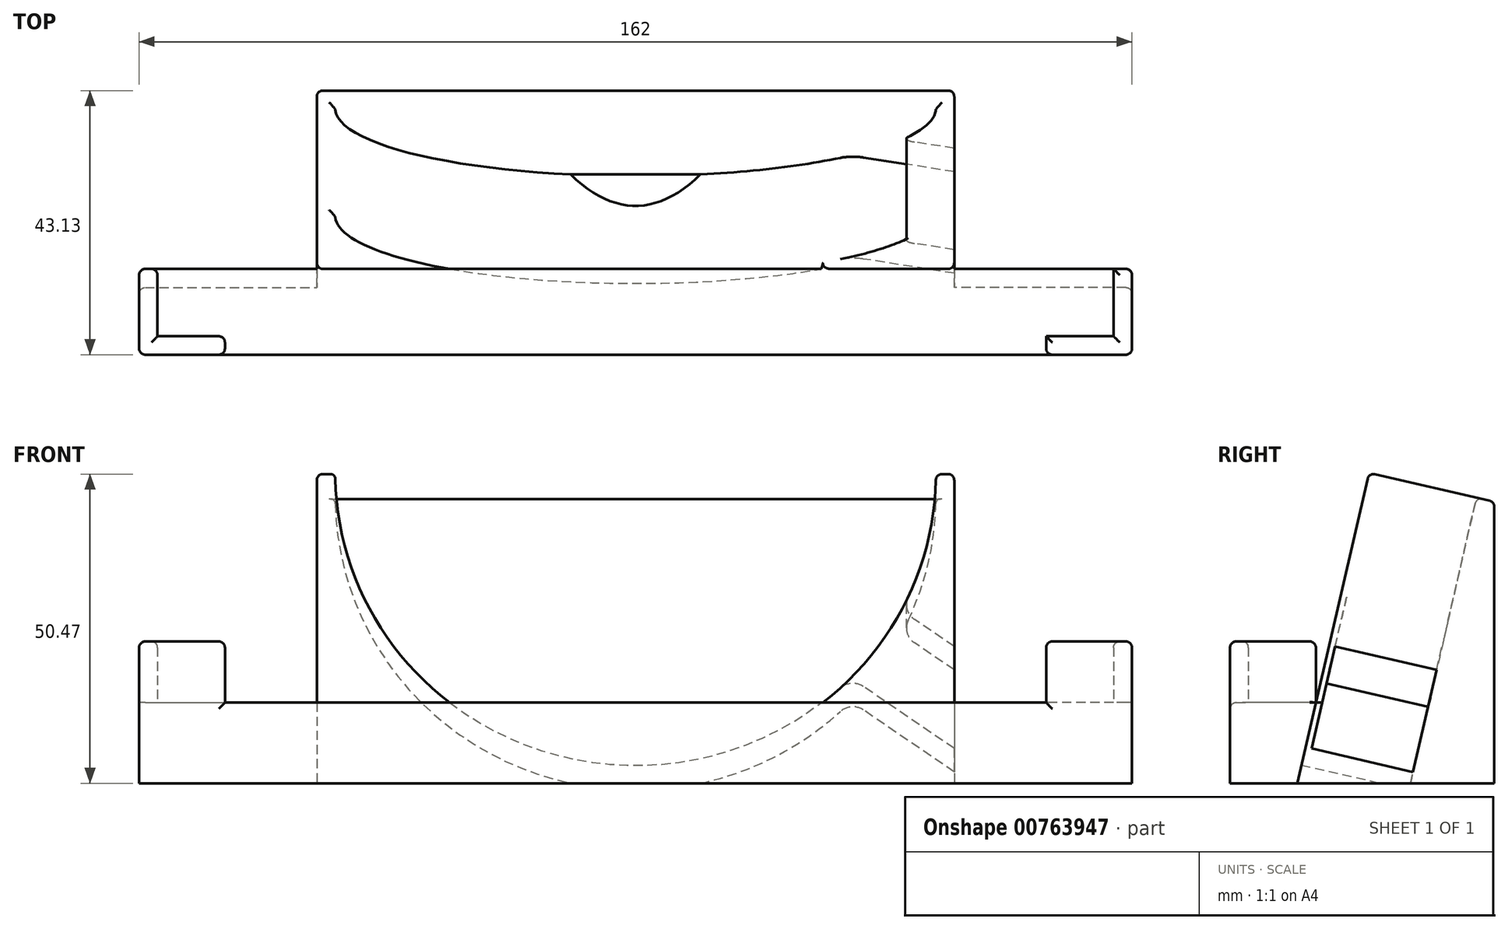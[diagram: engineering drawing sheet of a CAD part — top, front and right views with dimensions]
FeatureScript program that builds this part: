
annotation { "Feature Type Name" : "Feature", "Feature Type Description" : "" }
export const myFeature = defineFeature(function(context is Context, id is Id, definition is map)
    precondition{}
    {
        {
            var Q0;
            Q0=qCreatedBy(makeId("Right.planeOp"),FACE);
            var sketch = newSketch(context, id + "F0", { "sketchPlane" : qUnion([Q0])});
            skLineSegment(sketch, "E0", {"start": v(-55.45, -33.4) * mm, "end": v(107.34, -33.4) * mm});
            skLineSegment(sketch, "E1", {"start": v(-32.06, 67.93) * mm, "end": v(-11.6, 63.2) * mm});
            skLineSegment(sketch, "E2", {"start": v(-11.6, 63.2) * mm, "end": v(-11.6, -33.4) * mm});
            skLineSegment(sketch, "E3", {"start": v(-11.6, 63.2) * mm, "end": v(-33.9, -33.4) * mm});
            skLineSegment(sketch, "E4", {"start": v(-52.42, -20.25) * mm, "end": v(-66.42, -20.25) * mm});
            skLineSegment(sketch, "E5", {"start": v(-66.42, -20.25) * mm, "end": v(-66.42, -33.4) * mm});
            skLineSegment(sketch, "E6", {"start": v(-66.42, -33.4) * mm, "end": v(-47.42, -33.4) * mm});
            skLineSegment(sketch, "E7", {"start": v(-32.06, 67.93) * mm, "end": v(-55.45, -33.4) * mm});
            skLineSegment(sketch, "E8", {"start": v(-43.76, 17.26) * mm, "end": v(-23.3, 12.54) * mm});
            skLineSegment(sketch, "E9", {"start": v(-23.3, 12.54) * mm, "end": v(-23.3, -33.4) * mm});
            skSolve(sketch);
        }
        {
            var Q0;
            {var subQ3=sQuery(id+"F0.wireOp",EDGE,"E9");Q0=makeQuery(id+"F0.imprint","IMPRINT",FACE,{"disambiguationData":[TD([[makeQuery(id+"F0.imprint","IMPRINT",EDGE,{"derivedFrom":subQ3}),-1.0]])]});}
            var Q1;
            {var subQ2=sQuery(id+"F0.wireOp",EDGE,"E8");Q1=makeQuery(id+"F0.imprint","IMPRINT",FACE,{"disambiguationData":[TD([[makeQuery(id+"F0.imprint","IMPRINT",EDGE,{"derivedFrom":subQ2}),-1.0]])]});}
            extrude(context, id + "F1", {"entities" : qUnion([Q0, Q1]), "oppositeDirection" : true, "depth" : 52 * mm, "offsetDistance" : 25 * mm});
        }
        {
            var Q0;
            {var subQ3=sQuery(id+"F0.wireOp",EDGE,"E9");Q0=makeQuery(id+"F0.imprint","IMPRINT",FACE,{"disambiguationData":[TD([[makeQuery(id+"F0.imprint","IMPRINT",EDGE,{"derivedFrom":subQ3}),-1.0]])]});}
            var Q1;
            {var subQ2=sQuery(id+"F0.wireOp",EDGE,"E8");Q1=makeQuery(id+"F0.imprint","IMPRINT",FACE,{"disambiguationData":[TD([[makeQuery(id+"F0.imprint","IMPRINT",EDGE,{"derivedFrom":subQ2}),-1.0]])]});}
            extrude(context, id + "F2", {"entities" : qUnion([Q0, Q1]), "operationType" : NewBodyOperationType.ADD, "depth" : 52 * mm, "offsetDistance" : 25 * mm});
        }
        {
            var Q0;
            {var subQ0=sQuery(id+"F0.wireOp",EDGE,"E4");Q0=makeQuery(id+"F0.imprint","IMPRINT",FACE,{"disambiguationData":[TD([[makeQuery(id+"F0.imprint","IMPRINT",EDGE,{"derivedFrom":subQ0}),1.0]])]});}
            extrude(context, id + "F3", {"entities" : qUnion([Q0]), "operationType" : NewBodyOperationType.ADD, "depth" : 81 * mm, "offsetDistance" : 25 * mm});
        }
        {
            var Q0;
            {var subQ0=sQuery(id+"F0.wireOp",EDGE,"E4");Q0=makeQuery(id+"F0.imprint","IMPRINT",FACE,{"disambiguationData":[TD([[makeQuery(id+"F0.imprint","IMPRINT",EDGE,{"derivedFrom":subQ0}),1.0]])]});}
            extrude(context, id + "F4", {"entities" : qUnion([Q0]), "operationType" : NewBodyOperationType.ADD, "oppositeDirection" : true, "depth" : 81 * mm, "offsetDistance" : 25 * mm});
        }
        {
            var Q0;
            {var subQ0=sQuery(id+"F0.wireOp",EDGE,"E7");Q0=makeQuery(id+"F2.boolean.opBoolean","MERGE",FACE,{"derivedFrom":[makeQuery(id+"F1.opExtrude","SWEPT_FACE",FACE,{"disambiguationData":[OSD([subQ0])]}),makeQuery(id+"F2.opExtrude","SWEPT_FACE",FACE,{"disambiguationData":[OSD([subQ0])]})]});}
            var sketch = newSketch(context, id + "F5", { "sketchPlane" : qUnion([Q0])});
            skCircle(sketch, "E10", {"center": v(0, 6.98) * mm, "radius": 49 * mm});
            skSolve(sketch);
        }
        {
            var Q0;
            Q0=qSketchRegion(id+"F5",true);
            var Q1;
            {var subQ0=sQuery(id+"F5.wireOp",EDGE,"E10");var subQ1=sQuery(id+"F0.wireOp",EDGE,"E8");var subQ2=sQuery(id+"F0.wireOp",EDGE,"E7");var subQ3=makeQuery(id+"F2.boolean.opBoolean","MERGE",EDGE,{"derivedFrom":[makeQuery(id+"F1.opExtrude","SWEPT_EDGE",EDGE,{"disambiguationData":[OSD([subQ2,subQ1])]}),makeQuery(id+"F2.opExtrude","SWEPT_EDGE",EDGE,{"disambiguationData":[OSD([subQ2,subQ1])]})]});var subQ4=makeQuery(id+"F5.imprint","INTERSECT",VERTEX,{"disambiguationData":[OD(0.0)],"derivedFrom":[subQ3,subQ0]});Q1=makeQuery(id+"F5.imprint","IMPRINT",FACE,{"disambiguationData":[TD([[makeQuery(id+"F5.imprint","IMPRINT",EDGE,{"disambiguationData":[TD([[subQ4,-1.0]])],"derivedFrom":subQ0}),1.0]])]});}
            extrude(context, id + "F6", {"entities" : qUnion([Q0, Q1]), "operationType" : NewBodyOperationType.REMOVE, "oppositeDirection" : true, "depth" : 18 * mm, "offsetDistance" : 25 * mm});
        }
        {
            var Q0;
            {var subQ0=sQuery(id+"F0.wireOp",EDGE,"E4");Q0=makeQuery(id+"F4.boolean.opBoolean","MERGE",FACE,{"derivedFrom":[makeQuery(id+"F3.opExtrude","SWEPT_FACE",FACE,{"disambiguationData":[OSD([subQ0])]}),makeQuery(id+"F4.opExtrude","SWEPT_FACE",FACE,{"disambiguationData":[OSD([subQ0])]})]});}
            var sketch = newSketch(context, id + "F7", { "sketchPlane" : qUnion([Q0])});
            skLineSegment(sketch, "E11.bottom", {"start": v(-81, -52.42) * mm, "end": v(-78, -52.42) * mm});
            skLineSegment(sketch, "E11.top", {"start": v(-81, -66.42) * mm, "end": v(-78, -66.42) * mm});
            skLineSegment(sketch, "E11.left", {"start": v(-81, -52.42) * mm, "end": v(-81, -66.42) * mm});
            skLineSegment(sketch, "E11.right", {"start": v(-78, -52.42) * mm, "end": v(-78, -63.42) * mm});
            skLineSegment(sketch, "E12.bottom", {"start": v(-81, -66.42) * mm, "end": v(-67, -66.42) * mm});
            skLineSegment(sketch, "E12.top", {"start": v(-78, -63.42) * mm, "end": v(-67, -63.42) * mm});
            skLineSegment(sketch, "E12.left", {"start": v(-81, -66.42) * mm, "end": v(-81, -63.42) * mm});
            skLineSegment(sketch, "E12.right", {"start": v(-67, -66.42) * mm, "end": v(-67, -63.42) * mm});
            skLineSegment(sketch, "E13.bottom", {"start": v(81, -52.42) * mm, "end": v(78, -52.42) * mm});
            skLineSegment(sketch, "E13.top", {"start": v(81, -66.42) * mm, "end": v(78, -66.42) * mm});
            skLineSegment(sketch, "E13.left", {"start": v(81, -52.42) * mm, "end": v(81, -66.42) * mm});
            skLineSegment(sketch, "E13.right", {"start": v(78, -52.42) * mm, "end": v(78, -63.42) * mm});
            skLineSegment(sketch, "E14.bottom", {"start": v(81, -66.42) * mm, "end": v(67, -66.42) * mm});
            skLineSegment(sketch, "E14.top", {"start": v(78, -63.42) * mm, "end": v(67, -63.42) * mm});
            skLineSegment(sketch, "E14.left", {"start": v(81, -66.42) * mm, "end": v(81, -63.42) * mm});
            skLineSegment(sketch, "E14.right", {"start": v(67, -66.42) * mm, "end": v(67, -63.42) * mm});
            skSolve(sketch);
        }
        {
            var Q0;
            Q0=makeQuery(id+"F7.imprint","IMPRINT",FACE,{"disambiguationData":[TD([[makeQuery(id+"F7.imprint","IMPRINT",EDGE,{"derivedFrom":sQuery(id+"F7.wireOp",EDGE,"E11.bottom")}),-1.0]])]});
            var Q1;
            Q1=makeQuery(id+"F7.imprint","IMPRINT",FACE,{"disambiguationData":[TD([[makeQuery(id+"F7.imprint","IMPRINT",EDGE,{"derivedFrom":sQuery(id+"F7.wireOp",EDGE,"E13.bottom")}),1.0]])]});
            extrude(context, id + "F8", {"entities" : qUnion([Q0, Q1]), "operationType" : NewBodyOperationType.ADD, "depth" : 10 * mm, "offsetDistance" : 25 * mm});
        }
        {
            var Q0;
            {var subQ0=sQuery(id+"F0.wireOp",EDGE,"E9");var subQ1=sQuery(id+"F0.wireOp",EDGE,"E8");var subQ2=sQuery(id+"F0.wireOp",EDGE,"E3");Q0=makeQuery(id+"F2.boolean.opBoolean","MERGE",EDGE,{"derivedFrom":[makeQuery(id+"F1.opExtrude","SWEPT_EDGE",EDGE,{"disambiguationData":[OSD([subQ2,subQ1,subQ0])]}),makeQuery(id+"F2.opExtrude","SWEPT_EDGE",EDGE,{"disambiguationData":[OSD([subQ2,subQ1,subQ0])]})]});}
            var Q1;
            {var subQ0=sQuery(id+"F0.wireOp",EDGE,"E8");Q1=makeQuery(id+"F6.boolean.opBoolean","INTERSECT",EDGE,{"derivedFrom":[makeQuery(id+"F2.boolean.opBoolean","MERGE",FACE,{"derivedFrom":[makeQuery(id+"F1.opExtrude","SWEPT_FACE",FACE,{"disambiguationData":[OSD([subQ0])]}),makeQuery(id+"F2.opExtrude","SWEPT_FACE",FACE,{"disambiguationData":[OSD([subQ0])]})]}),makeQuery(id+"F6.opExtrude","CAP_FACE",FACE,{"disambiguationData":[OSD([sQuery(id+"F5.wireOp",EDGE,"E10")])],"isStart":false})]});}
            var Q2;
            Q2=makeQuery(id+"F1.opExtrude","CAP_EDGE",EDGE,{"disambiguationData":[OSD([sQuery(id+"F0.wireOp",EDGE,"E8")])],"isStart":false});
            var Q3;
            {var subQ0=sQuery(id+"F0.wireOp",EDGE,"E8");Q3=makeQuery(id+"F6.boolean.opBoolean","INTERSECT",EDGE,{"disambiguationData":[OD(0.0)],"derivedFrom":[makeQuery(id+"F2.boolean.opBoolean","MERGE",FACE,{"derivedFrom":[makeQuery(id+"F1.opExtrude","SWEPT_FACE",FACE,{"disambiguationData":[OSD([subQ0])]}),makeQuery(id+"F2.opExtrude","SWEPT_FACE",FACE,{"disambiguationData":[OSD([subQ0])]})]}),makeQuery(id+"F6.opExtrude","SWEPT_FACE",FACE,{"disambiguationData":[OSD([sQuery(id+"F5.wireOp",EDGE,"E10")])]})]});}
            var Q4;
            {var subQ0=sQuery(id+"F0.wireOp",EDGE,"E7");var subQ1=sQuery(id+"F5.wireOp",EDGE,"E10");Q4=makeQuery(id+"F6.boolean.opBoolean","COPY",EDGE,{"disambiguationData":[topologyDisambiguationEdgeConnected([makeQuery(id+"F1.opExtrude","SWEPT_FACE",FACE,{"disambiguationData":[OSD([subQ0])]}),makeQuery(id+"F2.opExtrude","SWEPT_FACE",FACE,{"disambiguationData":[OSD([subQ0])]}),makeQuery(id+"F6.opExtrude","SWEPT_FACE",FACE,{"disambiguationData":[OSD([subQ1])]})]),OD(1.0)],"derivedFrom":makeQuery(id+"F6.opExtrude","CAP_EDGE",EDGE,{"disambiguationData":[OSD([subQ1])],"isStart":true})});}
            var Q5;
            {var subQ0=sQuery(id+"F0.wireOp",EDGE,"E8");Q5=makeQuery(id+"F6.boolean.opBoolean","INTERSECT",EDGE,{"disambiguationData":[OD(1.0)],"derivedFrom":[makeQuery(id+"F2.boolean.opBoolean","MERGE",FACE,{"derivedFrom":[makeQuery(id+"F1.opExtrude","SWEPT_FACE",FACE,{"disambiguationData":[OSD([subQ0])]}),makeQuery(id+"F2.opExtrude","SWEPT_FACE",FACE,{"disambiguationData":[OSD([subQ0])]})]}),makeQuery(id+"F6.opExtrude","SWEPT_FACE",FACE,{"disambiguationData":[OSD([sQuery(id+"F5.wireOp",EDGE,"E10")])]})]});}
            var Q6;
            Q6=makeQuery(id+"F2.opExtrude","CAP_EDGE",EDGE,{"disambiguationData":[OSD([sQuery(id+"F0.wireOp",EDGE,"E9")])],"isStart":false});
            var Q7;
            {var subQ0=sQuery(id+"F0.wireOp",EDGE,"E7");var subQ1=sQuery(id+"F5.wireOp",EDGE,"E10");Q7=makeQuery(id+"F6.boolean.opBoolean","COPY",EDGE,{"disambiguationData":[topologyDisambiguationEdgeConnected([makeQuery(id+"F1.opExtrude","SWEPT_FACE",FACE,{"disambiguationData":[OSD([subQ0])]}),makeQuery(id+"F2.opExtrude","SWEPT_FACE",FACE,{"disambiguationData":[OSD([subQ0])]}),makeQuery(id+"F6.opExtrude","SWEPT_FACE",FACE,{"disambiguationData":[OSD([subQ1])]})]),OD(0.0)],"derivedFrom":makeQuery(id+"F6.opExtrude","CAP_EDGE",EDGE,{"disambiguationData":[OSD([subQ1])],"isStart":true})});}
            var Q8;
            Q8=makeQuery(id+"F8.opExtrude","CAP_EDGE",EDGE,{"disambiguationData":[OSD([sQuery(id+"F7.wireOp",EDGE,"E13.bottom")])],"isStart":false});
            var Q9;
            Q9=makeQuery(id+"F8.opExtrude","CAP_EDGE",EDGE,{"disambiguationData":[OSD([sQuery(id+"F7.wireOp",EDGE,"E14.top")])],"isStart":false});
            var Q10;
            Q10=makeQuery(id+"F8.opExtrude","CAP_EDGE",EDGE,{"disambiguationData":[OSD([sQuery(id+"F7.wireOp",EDGE,"E13.right")])],"isStart":false});
            var Q11;
            Q11=makeQuery(id+"F8.opExtrude","CAP_EDGE",EDGE,{"disambiguationData":[OSD([sQuery(id+"F7.wireOp",EDGE,"E14.right")])],"isStart":false});
            var Q12;
            Q12=makeQuery(id+"F8.opExtrude","CAP_EDGE",EDGE,{"disambiguationData":[OSD([sQuery(id+"F7.wireOp",EDGE,"E14.bottom")])],"isStart":false});
            var Q13;
            Q13=makeQuery(id+"F8.opExtrude","CAP_EDGE",EDGE,{"disambiguationData":[OSD([sQuery(id+"F7.wireOp",EDGE,"E13.left"),sQuery(id+"F7.wireOp",EDGE,"E14.left")])],"isStart":false});
            var Q14;
            {var subQ0=sQuery(id+"F0.wireOp",EDGE,"E5");var subQ1=sQuery(id+"F0.wireOp",EDGE,"E4");Q14=makeQuery(id+"F4.boolean.opBoolean","MERGE",EDGE,{"derivedFrom":[makeQuery(id+"F3.opExtrude","SWEPT_EDGE",EDGE,{"disambiguationData":[OSD([subQ1,subQ0])]}),makeQuery(id+"F4.opExtrude","SWEPT_EDGE",EDGE,{"disambiguationData":[OSD([subQ1,subQ0])]})]});}
            var Q15;
            Q15=makeQuery(id+"F8.opExtrude","SWEPT_EDGE",EDGE,{"disambiguationData":[OSD([sQuery(id+"F0.wireOp",EDGE,"E4"),sQuery(id+"F0.wireOp",EDGE,"E5"),sQuery(id+"F7.wireOp",EDGE,"E14.bottom"),sQuery(id+"F7.wireOp",EDGE,"E14.right")])]});
            var Q16;
            Q16=makeQuery(id+"F8.boolean.opBoolean","MERGE",EDGE,{"derivedFrom":[makeQuery(id+"F3.opExtrude","CAP_EDGE",EDGE,{"disambiguationData":[OSD([sQuery(id+"F0.wireOp",EDGE,"E5")])],"isStart":false}),makeQuery(id+"F8.opExtrude","SWEPT_EDGE",EDGE,{"disambiguationData":[OSD([sQuery(id+"F7.wireOp",EDGE,"E14.bottom"),sQuery(id+"F7.wireOp",EDGE,"E14.left")])]})]});
            var Q17;
            Q17=makeQuery(id+"F8.opExtrude","SWEPT_EDGE",EDGE,{"disambiguationData":[OSD([sQuery(id+"F0.wireOp",EDGE,"E4"),sQuery(id+"F0.wireOp",EDGE,"E5"),sQuery(id+"F7.wireOp",EDGE,"E12.bottom"),sQuery(id+"F7.wireOp",EDGE,"E12.right")])]});
            var Q18;
            Q18=makeQuery(id+"F8.opExtrude","CAP_EDGE",EDGE,{"disambiguationData":[OSD([sQuery(id+"F7.wireOp",EDGE,"E12.right")])],"isStart":false});
            var Q19;
            Q19=makeQuery(id+"F8.opExtrude","CAP_EDGE",EDGE,{"disambiguationData":[OSD([sQuery(id+"F7.wireOp",EDGE,"E12.top")])],"isStart":false});
            var Q20;
            Q20=makeQuery(id+"F8.opExtrude","CAP_EDGE",EDGE,{"disambiguationData":[OSD([sQuery(id+"F7.wireOp",EDGE,"E12.bottom")])],"isStart":false});
            var Q21;
            Q21=makeQuery(id+"F8.opExtrude","CAP_EDGE",EDGE,{"disambiguationData":[OSD([sQuery(id+"F7.wireOp",EDGE,"E11.left"),sQuery(id+"F7.wireOp",EDGE,"E12.left")])],"isStart":false});
            var Q22;
            Q22=makeQuery(id+"F8.opExtrude","CAP_EDGE",EDGE,{"disambiguationData":[OSD([sQuery(id+"F7.wireOp",EDGE,"E11.right")])],"isStart":false});
            var Q23;
            Q23=makeQuery(id+"F8.opExtrude","CAP_EDGE",EDGE,{"disambiguationData":[OSD([sQuery(id+"F7.wireOp",EDGE,"E11.bottom")])],"isStart":false});
            var Q24;
            Q24=makeQuery(id+"F8.boolean.opBoolean","MERGE",EDGE,{"derivedFrom":[makeQuery(id+"F4.opExtrude","CAP_EDGE",EDGE,{"disambiguationData":[OSD([sQuery(id+"F0.wireOp",EDGE,"E5")])],"isStart":false}),makeQuery(id+"F8.opExtrude","SWEPT_EDGE",EDGE,{"disambiguationData":[OSD([sQuery(id+"F7.wireOp",EDGE,"E12.bottom"),sQuery(id+"F7.wireOp",EDGE,"E12.left")])]})]});
            var Q25;
            {var subQ0=sQuery(id+"F0.wireOp",EDGE,"E7");Q25=makeQuery(id+"F3.boolean.opBoolean","SPLIT",EDGE,{"disambiguationData":[topologyDisambiguationEdgeConnected([makeQuery(id+"F1.opExtrude","SWEPT_FACE",FACE,{"disambiguationData":[OSD([subQ0])]})])],"derivedFrom":makeQuery(id+"F2.opExtrude","CAP_EDGE",EDGE,{"disambiguationData":[OSD([subQ0])],"isStart":false})});}
            var Q26;
            {var subQ0=sQuery(id+"F0.wireOp",EDGE,"E7");var subQ1=sQuery(id+"F0.wireOp",EDGE,"E8");Q26=makeQuery(id+"F6.boolean.opBoolean","SPLIT",EDGE,{"disambiguationData":[TD([makeQuery(id+"F2.opExtrude","CAP_FACE",FACE,{"disambiguationData":[OSD([sQuery(id+"F0.wireOp",EDGE,"E0"),sQuery(id+"F0.wireOp",EDGE,"E6"),subQ0,subQ1,sQuery(id+"F0.wireOp",EDGE,"E9")])],"isStart":false})])],"derivedFrom":makeQuery(id+"F2.boolean.opBoolean","MERGE",EDGE,{"derivedFrom":[makeQuery(id+"F1.opExtrude","SWEPT_EDGE",EDGE,{"disambiguationData":[OSD([subQ0,subQ1])]}),makeQuery(id+"F2.opExtrude","SWEPT_EDGE",EDGE,{"disambiguationData":[OSD([subQ0,subQ1])]})]})});}
            var Q27;
            Q27=makeQuery(id+"F2.opExtrude","CAP_EDGE",EDGE,{"disambiguationData":[OSD([sQuery(id+"F0.wireOp",EDGE,"E8")])],"isStart":false});
            var Q28;
            {var subQ0=sQuery(id+"F0.wireOp",EDGE,"E7");Q28=makeQuery(id+"F4.boolean.opBoolean","SPLIT",EDGE,{"disambiguationData":[topologyDisambiguationEdgeConnected([makeQuery(id+"F1.opExtrude","SWEPT_FACE",FACE,{"disambiguationData":[OSD([subQ0])]})])],"derivedFrom":makeQuery(id+"F1.opExtrude","CAP_EDGE",EDGE,{"disambiguationData":[OSD([subQ0])],"isStart":false})});}
            var Q29;
            {var subQ0=sQuery(id+"F0.wireOp",EDGE,"E7");var subQ1=sQuery(id+"F0.wireOp",EDGE,"E8");Q29=makeQuery(id+"F6.boolean.opBoolean","SPLIT",EDGE,{"disambiguationData":[TD([makeQuery(id+"F1.opExtrude","CAP_FACE",FACE,{"disambiguationData":[OSD([sQuery(id+"F0.wireOp",EDGE,"E0"),sQuery(id+"F0.wireOp",EDGE,"E6"),subQ0,subQ1,sQuery(id+"F0.wireOp",EDGE,"E9")])],"isStart":false})])],"derivedFrom":makeQuery(id+"F2.boolean.opBoolean","MERGE",EDGE,{"derivedFrom":[makeQuery(id+"F1.opExtrude","SWEPT_EDGE",EDGE,{"disambiguationData":[OSD([subQ0,subQ1])]}),makeQuery(id+"F2.opExtrude","SWEPT_EDGE",EDGE,{"disambiguationData":[OSD([subQ0,subQ1])]})]})});}
            var Q30;
            Q30=makeQuery(id+"F1.opExtrude","CAP_EDGE",EDGE,{"disambiguationData":[OSD([sQuery(id+"F0.wireOp",EDGE,"E9")])],"isStart":false});
            var Q31;
            Q31=makeQuery(id+"F8.opExtrude","SWEPT_EDGE",EDGE,{"disambiguationData":[OSD([sQuery(id+"F7.wireOp",EDGE,"E12.top"),sQuery(id+"F7.wireOp",EDGE,"E12.right")])]});
            var Q32;
            Q32=makeQuery(id+"F8.opExtrude","SWEPT_EDGE",EDGE,{"disambiguationData":[OSD([sQuery(id+"F0.wireOp",EDGE,"E4"),sQuery(id+"F0.wireOp",EDGE,"E7"),sQuery(id+"F7.wireOp",EDGE,"E11.bottom"),sQuery(id+"F7.wireOp",EDGE,"E11.right")])]});
            var Q33;
            Q33=makeQuery(id+"F8.opExtrude","SWEPT_EDGE",EDGE,{"disambiguationData":[OSD([sQuery(id+"F7.wireOp",EDGE,"E11.bottom"),sQuery(id+"F7.wireOp",EDGE,"E11.left")])]});
            var Q34;
            Q34=makeQuery(id+"F4.opExtrude","CAP_EDGE",EDGE,{"disambiguationData":[OSD([sQuery(id+"F0.wireOp",EDGE,"E7")])],"isStart":false});
            var Q35;
            Q35=makeQuery(id+"F8.opExtrude","SWEPT_EDGE",EDGE,{"disambiguationData":[OSD([sQuery(id+"F7.wireOp",EDGE,"E13.bottom"),sQuery(id+"F7.wireOp",EDGE,"E13.left")])]});
            var Q36;
            Q36=makeQuery(id+"F3.opExtrude","CAP_EDGE",EDGE,{"disambiguationData":[OSD([sQuery(id+"F0.wireOp",EDGE,"E7")])],"isStart":false});
            fillet(context, id + "F9", {"entities" : qUnion([Q0, Q1, Q2, Q3, Q4, Q5, Q6, Q7, Q8, Q9, Q10, Q11, Q12, Q13, Q14, Q15, Q16, Q17, Q18, Q19, Q20, Q21, Q22, Q23, Q24, Q25, Q26, Q27, Q28, Q29, Q30, Q31, Q32, Q33, Q34, Q35, Q36]), "radius" : 1 * mm, "tangentPropagation" : true, "allowEdgeOverflow" : false});
        }
        {
            var Q0;
            Q0=makeQuery(id+"F6.boolean.opBoolean","COPY",FACE,{"derivedFrom":makeQuery(id+"F6.opExtrude","CAP_FACE",FACE,{"disambiguationData":[OSD([sQuery(id+"F5.wireOp",EDGE,"E10")])],"isStart":false})});
            var sketch = newSketch(context, id + "F10", { "sketchPlane" : qUnion([Q0])});
            skLineSegment(sketch, "E15", {"start": v(0, 5.98) * mm, "end": v(39.66, -21.8) * mm});
            skLineSegment(sketch, "E16.0", {"start": v(-4.02, 0.24) * mm, "end": v(35.6, -27.5) * mm});
            skLineSegment(sketch, "E17.0", {"start": v(4.02, 11.7) * mm, "end": v(43.62, -16.02) * mm});
            skLineSegment(sketch, "E18", {"start": v(34.03, -26.4) * mm, "end": v(42.06, -14.93) * mm});
            skLineSegment(sketch, "E19", {"start": v(21.85, -17.87) * mm, "end": v(29.88, -6.4) * mm});
            skSolve(sketch);
        }
        {
            var Q0;
            {var subQ0=sQuery(id+"F10.wireOp",EDGE,"E19");var subQ1=sQuery(id+"F10.wireOp",EDGE,"E15");var subQ2=makeQuery(id+"F10.imprint","INTERSECT",VERTEX,{"derivedFrom":[subQ1,subQ0]});Q0=makeQuery(id+"F10.imprint","IMPRINT",FACE,{"disambiguationData":[TD([[makeQuery(id+"F10.imprint","IMPRINT",EDGE,{"disambiguationData":[TD([[subQ2,-1.0]])],"derivedFrom":subQ1}),-1.0]])]});}
            var Q1;
            {var subQ0=sQuery(id+"F10.wireOp",EDGE,"E19");var subQ1=sQuery(id+"F10.wireOp",EDGE,"E15");var subQ2=makeQuery(id+"F10.imprint","INTERSECT",VERTEX,{"derivedFrom":[subQ1,subQ0]});Q1=makeQuery(id+"F10.imprint","IMPRINT",FACE,{"disambiguationData":[TD([[makeQuery(id+"F10.imprint","IMPRINT",EDGE,{"disambiguationData":[TD([[subQ2,-1.0]])],"derivedFrom":subQ1}),1.0]])]});}
            extrude(context, id + "F11", {"entities" : qUnion([Q0, Q1]), "operationType" : NewBodyOperationType.ADD, "depth" : 17 * mm, "offsetDistance" : 25 * mm});
        }
        {
            var Q0;
            Q0=makeQuery(id+"F11.opExtrude","SWEPT_FACE",FACE,{"disambiguationData":[OSD([sQuery(id+"F10.wireOp",EDGE,"E19")])]});
            extrude(context, id + "F12", {"entities" : qUnion([Q0]), "operationType" : NewBodyOperationType.REMOVE, "oppositeDirection" : true, "depth" : 40 * mm, "offsetDistance" : 25 * mm});
        }
        {
            var Q0;
            Q0=makeQuery(id+"F12.boolean.opBoolean","INTERSECT",EDGE,{"derivedFrom":[makeQuery(id+"F6.boolean.opBoolean","COPY",FACE,{"derivedFrom":makeQuery(id+"F6.opExtrude","SWEPT_FACE",FACE,{"disambiguationData":[OSD([sQuery(id+"F5.wireOp",EDGE,"E10")])]})}),makeQuery(id+"F12.opExtrude","SWEPT_FACE",FACE,{"disambiguationData":[OSD([sQuery(id+"F10.wireOp",EDGE,"E16.0"),sQuery(id+"F10.wireOp",EDGE,"E19")])]})]});
            var Q1;
            Q1=makeQuery(id+"F12.boolean.opBoolean","INTERSECT",EDGE,{"derivedFrom":[makeQuery(id+"F6.boolean.opBoolean","COPY",FACE,{"derivedFrom":makeQuery(id+"F6.opExtrude","SWEPT_FACE",FACE,{"disambiguationData":[OSD([sQuery(id+"F5.wireOp",EDGE,"E10")])]})}),makeQuery(id+"F12.opExtrude","SWEPT_FACE",FACE,{"disambiguationData":[OSD([sQuery(id+"F10.wireOp",EDGE,"E17.0"),sQuery(id+"F10.wireOp",EDGE,"E19")])]})]});
            var Q2;
            Q2=makeQuery(id+"F12.boolean.opBoolean","INTERSECT",EDGE,{"derivedFrom":[makeQuery(id+"F1.opExtrude","CAP_FACE",FACE,{"disambiguationData":[OSD([sQuery(id+"F0.wireOp",EDGE,"E0"),sQuery(id+"F0.wireOp",EDGE,"E6"),sQuery(id+"F0.wireOp",EDGE,"E7"),sQuery(id+"F0.wireOp",EDGE,"E8"),sQuery(id+"F0.wireOp",EDGE,"E9")])],"isStart":false}),makeQuery(id+"F12.opExtrude","SWEPT_FACE",FACE,{"disambiguationData":[OSD([sQuery(id+"F10.wireOp",EDGE,"E16.0"),sQuery(id+"F10.wireOp",EDGE,"E19")])]})]});
            var Q3;
            Q3=makeQuery(id+"F12.boolean.opBoolean","INTERSECT",EDGE,{"derivedFrom":[makeQuery(id+"F1.opExtrude","CAP_FACE",FACE,{"disambiguationData":[OSD([sQuery(id+"F0.wireOp",EDGE,"E0"),sQuery(id+"F0.wireOp",EDGE,"E6"),sQuery(id+"F0.wireOp",EDGE,"E7"),sQuery(id+"F0.wireOp",EDGE,"E8"),sQuery(id+"F0.wireOp",EDGE,"E9")])],"isStart":false}),makeQuery(id+"F12.opExtrude","SWEPT_FACE",FACE,{"disambiguationData":[OSD([sQuery(id+"F10.wireOp",EDGE,"E17.0"),sQuery(id+"F10.wireOp",EDGE,"E19")])]})]});
            fillet(context, id + "F13", {"entities" : qUnion([Q0, Q1, Q2, Q3]), "radius" : 3 * mm, "tangentPropagation" : true, "allowEdgeOverflow" : false});
        }
    });
